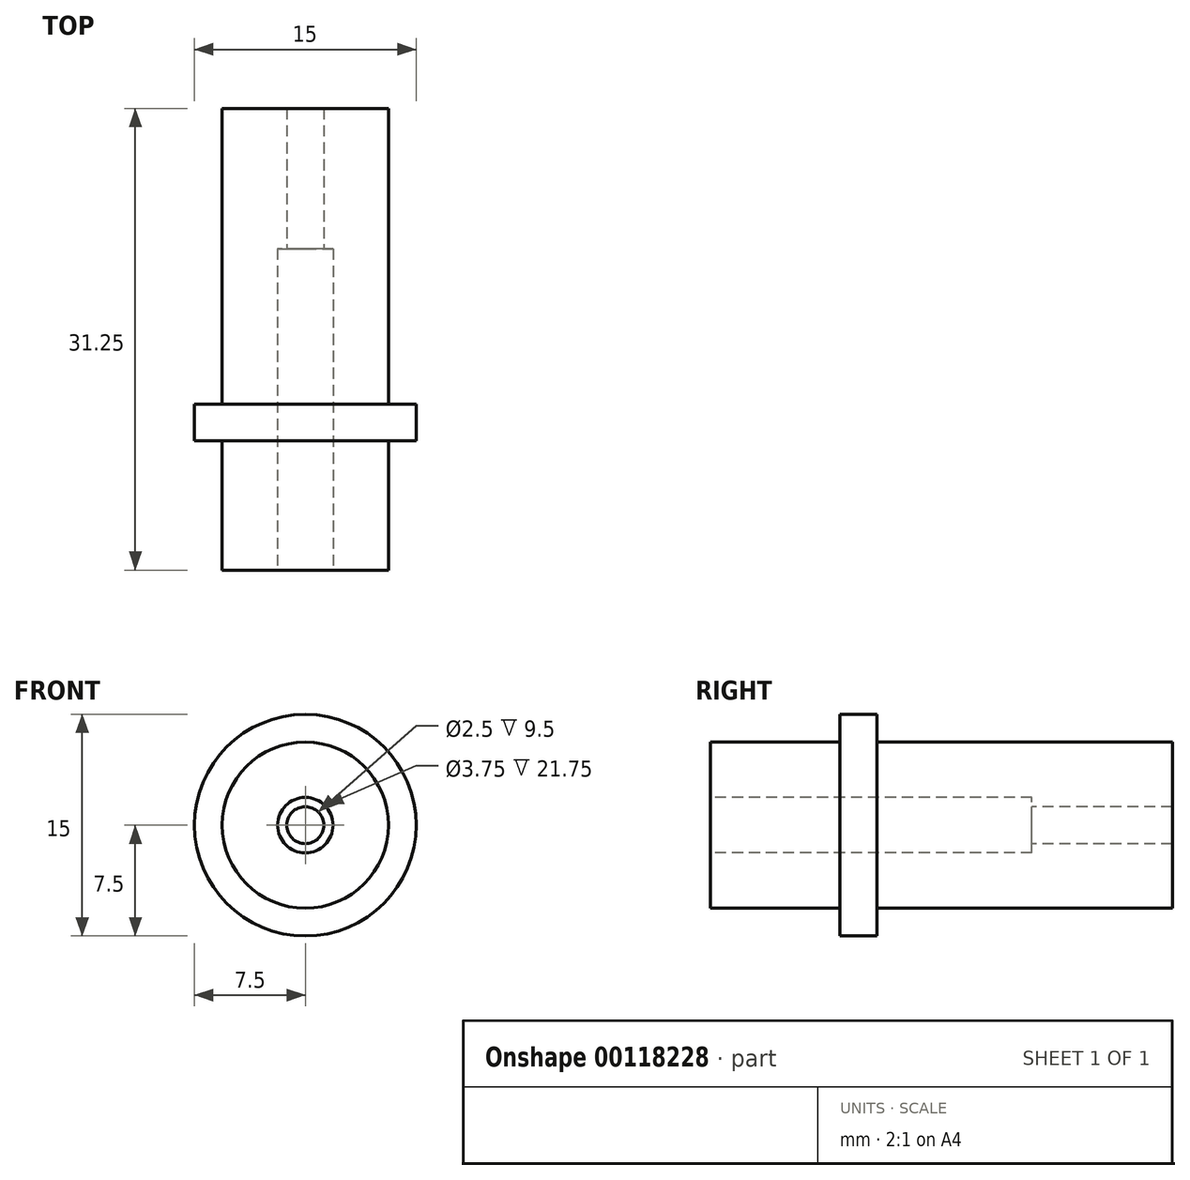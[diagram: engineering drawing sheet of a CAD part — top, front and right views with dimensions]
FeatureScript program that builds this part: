
annotation { "Feature Type Name" : "Feature", "Feature Type Description" : "" }
export const myFeature = defineFeature(function(context is Context, id is Id, definition is map)
    precondition{}
    {
        {
            var Q0;
            Q0=qCreatedBy(makeId("Front.planeOp"),FACE);
            var sketch = newSketch(context, id + "F0", { "sketchPlane" : qUnion([Q0])});
            skCircle(sketch, "E0", {"center": v(0, 0) * mm, "radius": 5.62 * mm});
            skSolve(sketch);
        }
        {
            var Q0;
            Q0 = qSketchRegion(id + "F0", true);
            extrude(context, id + "F1", {"entities" : qUnion([Q0]), "depth" : 31.25 * mm});
        }
        {
            var Q0;
            Q0=makeQuery(id+"F1.opExtrude","CAP_FACE",FACE,{"disambiguationData":[OSD([sQuery(id+"F0.wireOp",EDGE,"E0")])],"isStart":false});
            cPlane(context, id + "F2", {"entities" : qUnion([Q0]), "cplaneType" : CPlaneType.OFFSET, "offset" : 11.25 * mm, "oppositeDirection" : true, "width" : 150 * mm, "height" : 150 * mm});
        }
        {
            var Q0;
            Q0=qCreatedBy(id+"F2.planeOp",FACE);
            var sketch = newSketch(context, id + "F3", { "sketchPlane" : qUnion([Q0])});
            skCircle(sketch, "E1", {"center": v(0, 0) * mm, "radius": 7.5 * mm});
            skSolve(sketch);
        }
        {
            var Q0;
            Q0 = qSketchRegion(id + "F3", true);
            extrude(context, id + "F4", {"entities" : qUnion([Q0]), "operationType" : NewBodyOperationType.ADD, "depth" : 2.5 * mm});
        }
        {
            var Q0;
            Q0=makeQuery(id+"F1.opExtrude","CAP_FACE",FACE,{"disambiguationData":[OSD([sQuery(id+"F0.wireOp",EDGE,"E0")])],"isStart":false});
            var sketch = newSketch(context, id + "F5", { "sketchPlane" : qUnion([Q0])});
            skPoint(sketch, "E2", {"position": v(0, 0) * mm});
            skSolve(sketch);
        }
        {
            var Q0;
            Q0=sQuery(id+"F5.wireOp",VERTEX,"E2");
            var Q1;
            Q1=makeQuery(id+"F1.opExtrude","SWEPT_BODY",BODY,{"disambiguationData":[OSD([sQuery(id+"F0.wireOp",EDGE,"E0")])]});
            hole(context, id + "F6", {"style" : HoleStyle.C_BORE, "endStyle" : HoleEndStyle.BLIND, "holeDiameter" : 2.5 * mm, "cBoreDiameter" : 3.75 * mm, "cBoreDepth" : 21.75 * mm, "holeDepth" : 40 * mm, "startFromSketch" : true, "locations" : qUnion([Q0]), "scope" : qUnion([Q1])});
        }
    });
